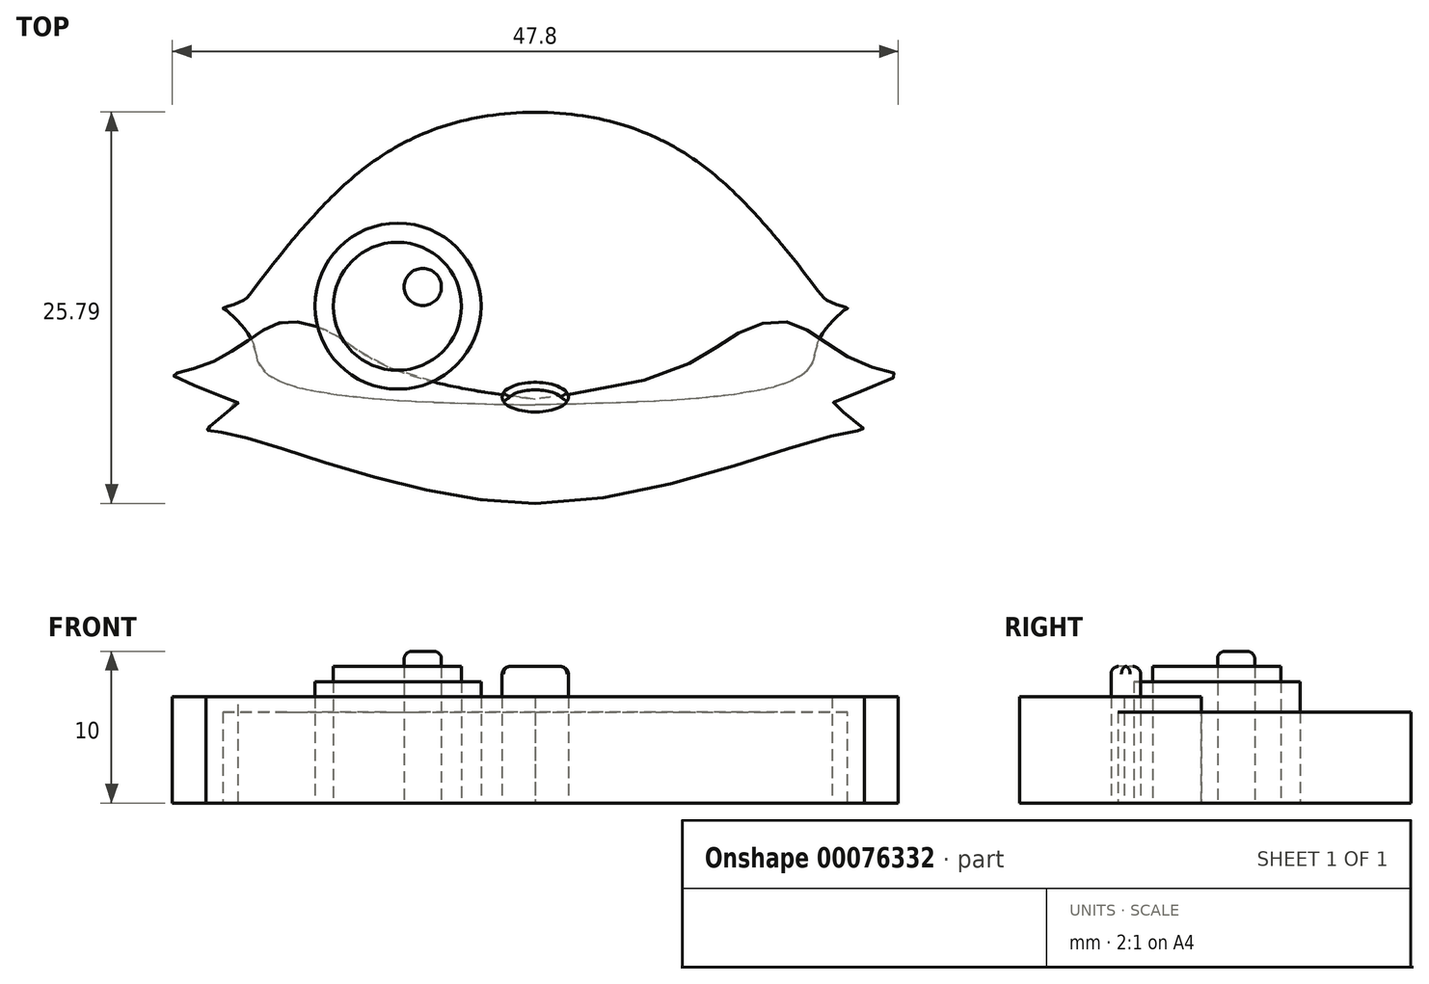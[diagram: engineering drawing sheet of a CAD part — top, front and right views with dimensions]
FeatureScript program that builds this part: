
annotation { "Feature Type Name" : "Feature", "Feature Type Description" : "" }
export const myFeature = defineFeature(function(context is Context, id is Id, definition is map)
    precondition{}
    {
        {
            var Q0;
            Q0=qCreatedBy(makeId("Top.planeOp"),FACE);
            var sketch = newSketch(context, id + "F0", { "sketchPlane" : qUnion([Q0])});
            skCircle(sketch, "E0", {"center": v(-7.4, 8.6) * mm, "radius": 1.22 * mm});
            skLineSegment(sketch, "E1", {"start": v(0, 0) * mm, "end": v(0, 16.53) * mm});
            skCircle(sketch, "E2.MirrorC", {"center": v(7.4, 8.6) * mm, "radius": 1.22 * mm});
            skSolve(sketch);
        }
        {
            var Q0;
            Q0=qCreatedBy(makeId("Top.planeOp"),FACE);
            var sketch = newSketch(context, id + "F1", { "sketchPlane" : qUnion([Q0])});
            skCircle(sketch, "E3", {"center": v(-9.08, 7.32) * mm, "radius": 4.22 * mm});
            skPoint(sketch, "E3.first.point", {"position": v(-12.4, 4.71) * mm});
            skPoint(sketch, "E3.second.point", {"position": v(-4.86, 7.48) * mm});
            skPoint(sketch, "E3.third.point", {"position": v(-9.19, 11.54) * mm});
            skCircle(sketch, "E4.MirrorC", {"center": v(9.08, 7.32) * mm, "radius": 4.22 * mm});
            skSolve(sketch);
        }
        {
            var Q0;
            Q0=qCreatedBy(makeId("Top.planeOp"),FACE);
            var sketch = newSketch(context, id + "F2", { "sketchPlane" : qUnion([Q0])});
            skCircle(sketch, "E5", {"center": v(-9.04, 7.33) * mm, "radius": 5.47 * mm});
            skPoint(sketch, "E5.first.point", {"position": v(-11.97, 2.7) * mm});
            skPoint(sketch, "E5.second.point", {"position": v(-3.59, 6.91) * mm});
            skPoint(sketch, "E5.third.point", {"position": v(-11.23, 12.35) * mm});
            skCircle(sketch, "E6.MirrorC", {"center": v(9.04, 7.33) * mm, "radius": 5.47 * mm});
            skSolve(sketch);
        }
        {
            var Q0;
            Q0=qCreatedBy(makeId("Top.planeOp"),FACE);
            var sketch = newSketch(context, id + "F3", { "sketchPlane" : qUnion([Q0])});
            skEllipse(sketch, "E7", {"center": v(0, 1.33) * mm, "majorRadius": 2.18 * mm, "minorRadius": 0.98 * mm, "majorAxis": v(-1, 0)});
            skSolve(sketch);
        }
        {
            var Q0;
            Q0=qCreatedBy(makeId("Top.planeOp"),FACE);
            var sketch = newSketch(context, id + "F4", { "sketchPlane" : qUnion([Q0])});
            skFitSpline(sketch, "E8", {"points": [v(0, -5.67) * mm, v(-19.42, -1.25) * mm, v(-21.67, -0.83) * mm, v(-21.65, -0.78) * mm, v(-19.57, 0.94) * mm, v(-19.57, 0.95) * mm, v(-23.84, 2.74) * mm, v(-23.88, 2.83) * mm, v(-21.76, 3.45) * mm, v(-18.79, 5.17) * mm, v(-16.36, 6.3) * mm, v(-13.12, 5.4) * mm, v(0, 1.21) * mm], "startDerivative": vector(-103.07, 0) * mm, "endDerivative": vector(169.56, -18.53) * mm});
            skLineSegment(sketch, "E9", {"start": v(0, 1.21) * mm, "end": v(0, -5.67) * mm});
            skFitSpline(sketch, "E10.MirrorCS", {"points": [v(0, -5.67) * mm, v(19.42, -1.25) * mm, v(21.67, -0.83) * mm, v(21.65, -0.78) * mm, v(19.57, 0.94) * mm, v(19.57, 0.95) * mm, v(23.84, 2.74) * mm, v(23.88, 2.83) * mm, v(21.76, 3.45) * mm, v(18.79, 5.17) * mm, v(16.36, 6.3) * mm, v(13.12, 5.4) * mm, v(0, 1.21) * mm], "startDerivative": vector(103.07, 0) * mm, "endDerivative": vector(-169.56, -18.53) * mm});
            skSolve(sketch);
        }
        {
            var Q0;
            Q0=qCreatedBy(makeId("Top.planeOp"),FACE);
            var sketch = newSketch(context, id + "F5", { "sketchPlane" : qUnion([Q0])});
            skFitSpline(sketch, "E11", {"points": [v(0, 20.12) * mm, v(-14.42, 13.48) * mm, v(-18.6, 8.38) * mm, v(-19.47, 7.59) * mm, v(-20.57, 7.2) * mm, v(-20.48, 7.15) * mm, v(-19.65, 6.4) * mm, v(-18.6, 4.9) * mm, v(-17.67, 2.84) * mm, v(0, 0.82) * mm], "startDerivative": vector(-96, -1.14) * mm, "endDerivative": vector(85.28, -1.74) * mm});
            skFitSpline(sketch, "E12.MirrorCS", {"points": [v(0, 20.12) * mm, v(14.42, 13.48) * mm, v(18.6, 8.38) * mm, v(19.47, 7.59) * mm, v(20.57, 7.2) * mm, v(20.48, 7.15) * mm, v(19.65, 6.4) * mm, v(18.6, 4.9) * mm, v(17.67, 2.84) * mm, v(0, 0.82) * mm], "startDerivative": vector(96, -1.14) * mm, "endDerivative": vector(-85.28, -1.74) * mm});
            skFitSpline(sketch, "E13", {"points": [v(-16.36, 11.24) * mm, v(-18.99, 16.33) * mm, v(-19.08, 19.68) * mm, v(-18.5, 22.79) * mm, v(-17.72, 24.95) * mm, v(-17.65, 24.95) * mm, v(-15.93, 24.41) * mm, v(-13.33, 23.26) * mm, v(-11.2, 22.01) * mm, v(-7.94, 18.45) * mm], "startDerivative": vector(-32.88, 36.97) * mm, "endDerivative": vector(22, -40.03) * mm});
            skFitSpline(sketch, "E14", {"points": [v(-15, 12.84) * mm, v(-15.96, 15.97) * mm, v(-15.8, 18.84) * mm, v(-15.19, 20.97) * mm, v(-15.09, 20.93) * mm, v(-13.7, 20.36) * mm, v(-12.25, 19.48) * mm, v(-9.82, 17.42) * mm], "startDerivative": vector(-8.98, 16) * mm, "endDerivative": vector(16.33, -18.57) * mm});
            skFitSpline(sketch, "E15.MirrorCS", {"points": [v(15, 12.84) * mm, v(15.96, 15.97) * mm, v(15.8, 18.84) * mm, v(15.19, 20.97) * mm, v(15.09, 20.93) * mm, v(13.7, 20.36) * mm, v(12.25, 19.48) * mm, v(9.82, 17.42) * mm], "startDerivative": vector(8.98, 16) * mm, "endDerivative": vector(-16.33, -18.57) * mm});
            skFitSpline(sketch, "E16.MirrorCS", {"points": [v(16.36, 11.24) * mm, v(18.99, 16.33) * mm, v(19.08, 19.68) * mm, v(18.5, 22.79) * mm, v(17.72, 24.95) * mm, v(17.65, 24.95) * mm, v(15.93, 24.41) * mm, v(13.33, 23.26) * mm, v(11.2, 22.01) * mm, v(7.94, 18.45) * mm], "startDerivative": vector(32.88, 36.97) * mm, "endDerivative": vector(-22, -40.03) * mm});
            skSolve(sketch);
        }
        {
            var Q0;
            Q0=makeQuery(id+"F0.imprint","IMPRINT",FACE,{"disambiguationData":[TD([[makeQuery(id+"F0.imprint","IMPRINT",EDGE,{"derivedFrom":sQuery(id+"F0.wireOp",EDGE,"E2.MirrorC")}),-1.0]])]});
            var Q1;
            Q1=makeQuery(id+"F0.imprint","IMPRINT",FACE,{"disambiguationData":[TD([[makeQuery(id+"F0.imprint","IMPRINT",EDGE,{"derivedFrom":sQuery(id+"F0.wireOp",EDGE,"E0")}),1.0]])]});
            extrude(context, id + "F6", {"entities" : qUnion([Q0, Q1]), "depth" : 10 * mm});
        }
        {
            var Q0;
            Q0=makeQuery(id+"F1.imprint","IMPRINT",FACE,{"disambiguationData":[TD([[makeQuery(id+"F1.imprint","IMPRINT",EDGE,{"derivedFrom":sQuery(id+"F1.wireOp",EDGE,"E3")}),1.0]])]});
            var Q1;
            Q1=makeQuery(id+"F1.imprint","IMPRINT",FACE,{"disambiguationData":[TD([[makeQuery(id+"F1.imprint","IMPRINT",EDGE,{"derivedFrom":sQuery(id+"F1.wireOp",EDGE,"E4.MirrorC")}),-1.0]])]});
            extrude(context, id + "F7", {"entities" : qUnion([Q0, Q1]), "depth" : 9 * mm});
        }
        {
            var Q0;
            Q0=makeQuery(id+"F2.imprint","IMPRINT",FACE,{"disambiguationData":[TD([[makeQuery(id+"F2.imprint","IMPRINT",EDGE,{"derivedFrom":sQuery(id+"F2.wireOp",EDGE,"E5")}),1.0]])]});
            var Q1;
            Q1=makeQuery(id+"F2.imprint","IMPRINT",FACE,{"disambiguationData":[TD([[makeQuery(id+"F2.imprint","IMPRINT",EDGE,{"derivedFrom":sQuery(id+"F2.wireOp",EDGE,"E6.MirrorC")}),-1.0]])]});
            extrude(context, id + "F8", {"entities" : qUnion([Q0, Q1]), "depth" : 8 * mm});
        }
        {
            var Q0;
            Q0=makeQuery(id+"F3.imprint","IMPRINT",FACE,{"disambiguationData":[TD([[makeQuery(id+"F3.imprint","IMPRINT",EDGE,{"derivedFrom":sQuery(id+"F3.wireOp",EDGE,"E7")}),1.0]])]});
            extrude(context, id + "F9", {"entities" : qUnion([Q0]), "depth" : 9 * mm});
        }
        {
            var Q0;
            Q0=makeQuery(id+"F5.imprint","IMPRINT",FACE,{"disambiguationData":[TD([[makeQuery(id+"F5.imprint","IMPRINT",EDGE,{"derivedFrom":sQuery(id+"F5.wireOp",EDGE,"E11")}),1.0]])]});
            extrude(context, id + "F10", {"entities" : qUnion([Q0]), "depth" : 6 * mm});
        }
        {
            var Q0;
            Q0=makeQuery(id+"F4.imprint","IMPRINT",FACE,{"disambiguationData":[TD([[makeQuery(id+"F4.imprint","IMPRINT",EDGE,{"derivedFrom":sQuery(id+"F4.wireOp",EDGE,"E8")}),-1.0]])]});
            var Q1;
            Q1=makeQuery(id+"F4.imprint","IMPRINT",FACE,{"disambiguationData":[TD([[makeQuery(id+"F4.imprint","IMPRINT",EDGE,{"derivedFrom":sQuery(id+"F4.wireOp",EDGE,"E9")}),1.0]])]});
            extrude(context, id + "F11", {"entities" : qUnion([Q0, Q1]), "depth" : 7 * mm});
        }
        {
            var Q0;
            Q0=makeQuery(id+"F9.opExtrude","CAP_EDGE",EDGE,{"disambiguationData":[OSD([sQuery(id+"F3.wireOp",EDGE,"E7")])],"isStart":false});
            var Q1;
            Q1=makeQuery(id+"F6.opExtrude","CAP_EDGE",EDGE,{"disambiguationData":[OSD([sQuery(id+"F0.wireOp",EDGE,"E2.MirrorC")])],"isStart":false});
            var Q2;
            Q2=makeQuery(id+"F6.opExtrude","CAP_EDGE",EDGE,{"disambiguationData":[OSD([sQuery(id+"F0.wireOp",EDGE,"E0")])],"isStart":false});
            fillet(context, id + "F12", {"entities" : qUnion([Q0, Q1, Q2]), "radius" : .5 * mm, "tangentPropagation" : true, "allowEdgeOverflow" : false});
        }
    });
